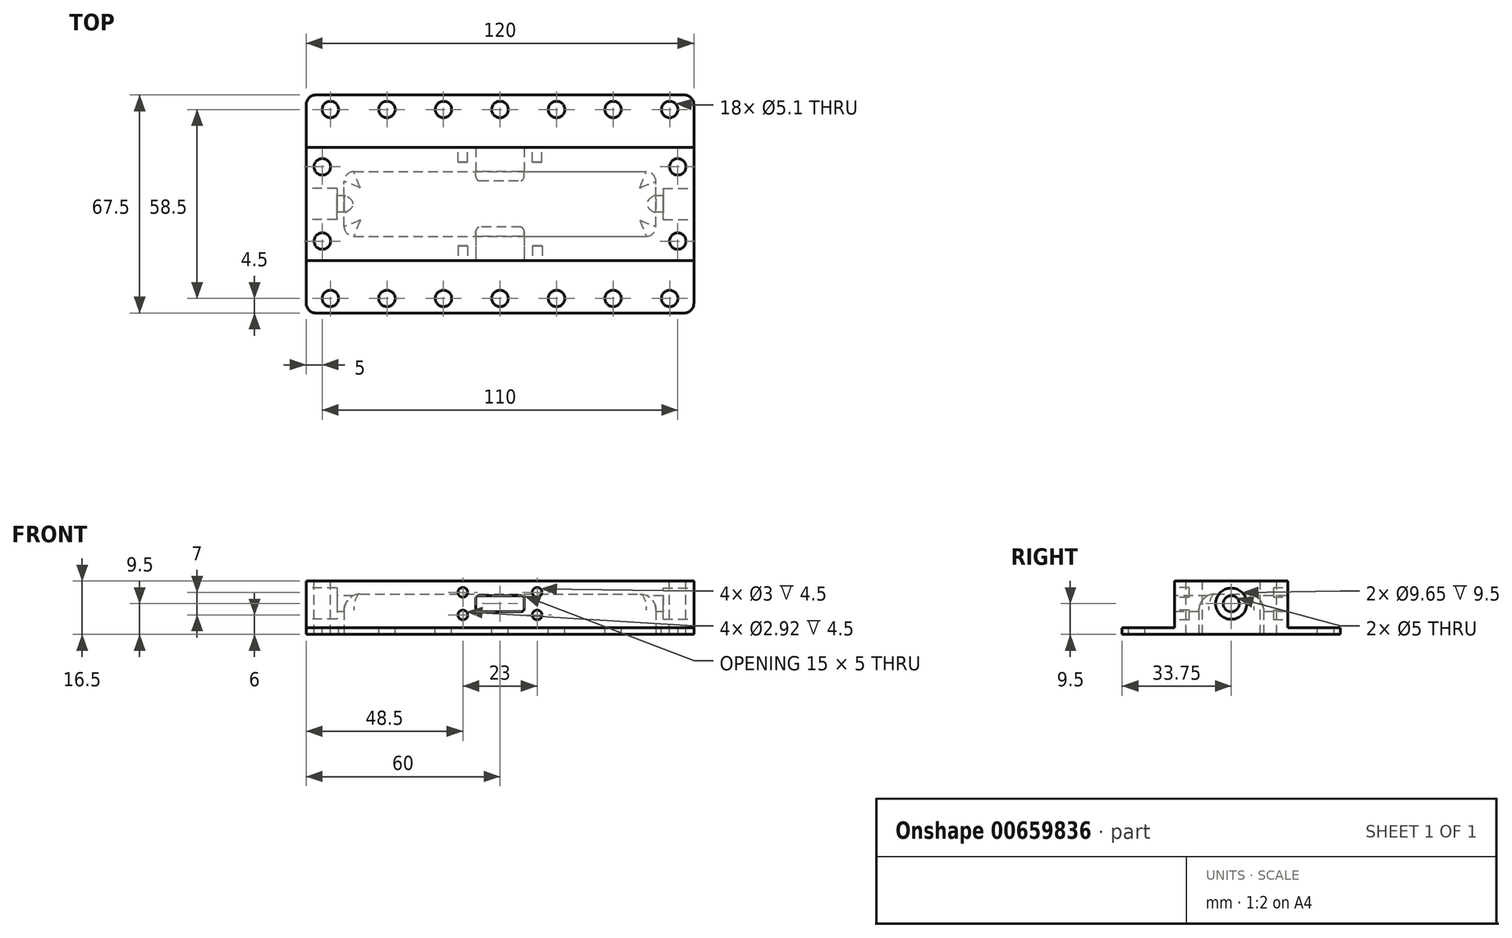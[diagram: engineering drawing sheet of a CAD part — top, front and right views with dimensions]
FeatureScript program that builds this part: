
annotation { "Feature Type Name" : "Feature", "Feature Type Description" : "" }
export const myFeature = defineFeature(function(context is Context, id is Id, definition is map)
    precondition{}
    {
        {
            var Q0;
            Q0=qCreatedBy(makeId("Top.planeOp"),FACE);
            var sketch = newSketch(context, id + "F0", { "sketchPlane" : qUnion([Q0])});
            skLineSegment(sketch, "E0.bottom", {"start": v(0, 0) * mm, "end": v(120, 0) * mm});
            skLineSegment(sketch, "E0.top", {"start": v(0, -67.5) * mm, "end": v(120, -67.5) * mm});
            skLineSegment(sketch, "E0.left", {"start": v(0, -67.5) * mm, "end": v(0, 0) * mm});
            skLineSegment(sketch, "E0.right", {"start": v(120, -67.5) * mm, "end": v(120, 0) * mm});
            skSolve(sketch);
        }
        {
            var Q0;
            Q0 = qSketchRegion(id + "F0", true);
            extrude(context, id + "F1", {"entities" : qUnion([Q0]), "oppositeDirection" : true, "depth" : 16.5 * mm, "offsetDistance" : 25 * mm});
        }
        {
            var Q0;
            Q0=makeQuery(id+"F1.opExtrude","CAP_FACE",FACE,{"disambiguationData":[OSD([sQuery(id+"F0.wireOp",EDGE,"E0.bottom"),sQuery(id+"F0.wireOp",EDGE,"E0.top"),sQuery(id+"F0.wireOp",EDGE,"E0.left"),sQuery(id+"F0.wireOp",EDGE,"E0.right")])],"isStart":false});
            var sketch = newSketch(context, id + "F2", { "sketchPlane" : qUnion([Q0])});
            skLineSegment(sketch, "E1.bottom", {"start": v(11.75, 43.75) * mm, "end": v(108.25, 43.75) * mm});
            skLineSegment(sketch, "E1.top", {"start": v(11.75, 23.75) * mm, "end": v(108.25, 23.75) * mm});
            skLineSegment(sketch, "E1.left", {"start": v(11.75, 43.75) * mm, "end": v(11.75, 23.75) * mm});
            skLineSegment(sketch, "E1.right", {"start": v(108.25, 43.75) * mm, "end": v(108.25, 23.75) * mm});
            skSolve(sketch);
        }
        {
            var Q0;
            Q0 = qSketchRegion(id + "F2", true);
            extrude(context, id + "F3", {"entities" : qUnion([Q0]), "operationType" : NewBodyOperationType.REMOVE, "oppositeDirection" : true, "depth" : 12.5 * mm, "offsetDistance" : 25 * mm});
        }
        {
            var Q0;
            Q0=makeQuery(id+"F1.opExtrude","CAP_FACE",FACE,{"disambiguationData":[OSD([sQuery(id+"F0.wireOp",EDGE,"E0.bottom"),sQuery(id+"F0.wireOp",EDGE,"E0.top"),sQuery(id+"F0.wireOp",EDGE,"E0.left"),sQuery(id+"F0.wireOp",EDGE,"E0.right")])],"isStart":true});
            var sketch = newSketch(context, id + "F4", { "sketchPlane" : qUnion([Q0])});
            skLineSegment(sketch, "E2.bottom", {"start": v(0, -16.25) * mm, "end": v(120, -16.25) * mm});
            skLineSegment(sketch, "E2.top", {"start": v(0, -51.25) * mm, "end": v(120, -51.25) * mm});
            skLineSegment(sketch, "E2.left", {"start": v(0, -16.25) * mm, "end": v(0, -51.25) * mm});
            skLineSegment(sketch, "E2.right", {"start": v(120, -16.25) * mm, "end": v(120, -51.25) * mm});
            skSolve(sketch);
        }
        {
            var Q0;
            Q0=makeQuery(id+"F4.imprint","IMPRINT",FACE,{"disambiguationData":[TD([[makeQuery(id+"F4.imprint","IMPRINT",EDGE,{"derivedFrom":sQuery(id+"F4.wireOp",EDGE,"E2.bottom")}),1.0]])]});
            var Q1;
            {var subQ0=sQuery(id+"F4.wireOp",EDGE,"E2.top");Q1=makeQuery(id+"F4.imprint","IMPRINT",FACE,{"disambiguationData":[TD([[makeQuery(id+"F4.imprint","IMPRINT",EDGE,{"derivedFrom":subQ0}),-1.0]])]});}
            extrude(context, id + "F5", {"entities" : qUnion([Q0, Q1]), "operationType" : NewBodyOperationType.REMOVE, "oppositeDirection" : true, "depth" : 14.5 * mm, "offsetDistance" : 25 * mm});
        }
        {
            var Q0;
            Q0=makeQuery(id+"F5.boolean.opBoolean","COPY",FACE,{"derivedFrom":makeQuery(id+"F5.opExtrude","SWEPT_FACE",FACE,{"disambiguationData":[OSD([sQuery(id+"F4.wireOp",EDGE,"E2.top")])]})});
            var sketch = newSketch(context, id + "F6", { "sketchPlane" : qUnion([Q0])});
            skLineSegment(sketch, "E3.bottom", {"start": v(52.5, -4.5) * mm, "end": v(67.5, -4.5) * mm});
            skLineSegment(sketch, "E3.top", {"start": v(52.5, -9.5) * mm, "end": v(67.5, -9.5) * mm});
            skLineSegment(sketch, "E3.left", {"start": v(52.5, -4.5) * mm, "end": v(52.5, -9.5) * mm});
            skLineSegment(sketch, "E3.right", {"start": v(67.5, -4.5) * mm, "end": v(67.5, -9.5) * mm});
            skSolve(sketch);
        }
        {
            var Q0;
            Q0 = qSketchRegion(id + "F6", true);
            extrude(context, id + "F7", {"entities" : qUnion([Q0]), "operationType" : NewBodyOperationType.REMOVE, "oppositeDirection" : true, "depth" : 39.7 * mm, "offsetDistance" : 25 * mm});
        }
        {
            var Q0;
            Q0=makeQuery(id+"F5.boolean.opBoolean","COPY",FACE,{"derivedFrom":makeQuery(id+"F5.opExtrude","CAP_FACE",FACE,{"disambiguationData":[OSD([sQuery(id+"F0.wireOp",EDGE,"E0.bottom"),sQuery(id+"F0.wireOp",EDGE,"E0.top"),sQuery(id+"F0.wireOp",EDGE,"E0.left"),sQuery(id+"F0.wireOp",EDGE,"E0.right"),sQuery(id+"F4.wireOp",EDGE,"E2.bottom"),sQuery(id+"F4.wireOp",EDGE,"E2.top"),sQuery(id+"F4.wireOp",EDGE,"E2.left"),sQuery(id+"F4.wireOp",EDGE,"E2.right")])],"isStart":false})});
            var sketch = newSketch(context, id + "F8", { "sketchPlane" : qUnion([Q0])});
            skCircle(sketch, "E4", {"center": v(7.5, -63) * mm, "radius": 2.55 * mm});
            skCircle(sketch, "E5.0.1.0", {"center": v(7.5, -4.5) * mm, "radius": 2.55 * mm});
            skCircle(sketch, "E5.1.0.0", {"center": v(25, -63) * mm, "radius": 2.55 * mm});
            skCircle(sketch, "E5.1.1.0", {"center": v(25, -4.5) * mm, "radius": 2.55 * mm});
            skCircle(sketch, "E5.2.0.0", {"center": v(42.5, -63) * mm, "radius": 2.55 * mm});
            skCircle(sketch, "E5.2.1.0", {"center": v(42.5, -4.5) * mm, "radius": 2.55 * mm});
            skLineSegment(sketch, "E5.direction1", {"start": v(7.5, -63) * mm, "end": v(25, -63) * mm, "construction": true});
            skLineSegment(sketch, "E5.direction2", {"start": v(7.5, -63) * mm, "end": v(7.5, -4.5) * mm, "construction": true});
            skCircle(sketch, "E6.0.3.0", {"center": v(60, -63) * mm, "radius": 2.55 * mm});
            skCircle(sketch, "E6.0.3.1", {"center": v(60, -4.5) * mm, "radius": 2.55 * mm});
            skCircle(sketch, "E6.0.4.0", {"center": v(77.5, -63) * mm, "radius": 2.55 * mm});
            skCircle(sketch, "E6.0.4.1", {"center": v(77.5, -4.5) * mm, "radius": 2.55 * mm});
            skCircle(sketch, "E6.0.5.0", {"center": v(95, -63) * mm, "radius": 2.55 * mm});
            skCircle(sketch, "E6.0.5.1", {"center": v(95, -4.5) * mm, "radius": 2.55 * mm});
            skCircle(sketch, "E6.0.6.0", {"center": v(112.5, -63) * mm, "radius": 2.55 * mm});
            skCircle(sketch, "E6.0.6.1", {"center": v(112.5, -4.5) * mm, "radius": 2.55 * mm});
            skCircle(sketch, "E7.2.0.0", {"center": v(240.5, -30) * mm, "radius": 1.6 * mm});
            skCircle(sketch, "E7.2.1.0", {"center": v(240.5, -10) * mm, "radius": 1.6 * mm});
            skSolve(sketch);
        }
        {
            var Q0;
            Q0 = qSketchRegion(id + "F8", true);
            extrude(context, id + "F9", {"entities" : qUnion([Q0]), "operationType" : NewBodyOperationType.REMOVE, "oppositeDirection" : true, "depth" : 25 * mm, "offsetDistance" : 25 * mm});
        }
        {
            var Q0;
            Q0=makeQuery(id+"F5.boolean.opBoolean","COPY",FACE,{"derivedFrom":makeQuery(id+"F5.opExtrude","SWEPT_FACE",FACE,{"disambiguationData":[OSD([sQuery(id+"F4.wireOp",EDGE,"E2.top")])]})});
            var sketch = newSketch(context, id + "F10", { "sketchPlane" : qUnion([Q0])});
            skCircle(sketch, "E8.1.0.0", {"center": v(48.5, -3.5) * mm, "radius": 1.5 * mm});
            skCircle(sketch, "E9.0.1.0", {"center": v(48.5, -10.5) * mm, "radius": 1.5 * mm});
            skCircle(sketch, "E9.1.0.0", {"center": v(71.5, -3.5) * mm, "radius": 1.5 * mm});
            skCircle(sketch, "E9.1.1.0", {"center": v(71.5, -10.5) * mm, "radius": 1.5 * mm});
            skLineSegment(sketch, "E9.direction1", {"start": v(48.5, -3.5) * mm, "end": v(71.5, -3.5) * mm, "construction": true});
            skLineSegment(sketch, "E9.direction2", {"start": v(48.5, -3.5) * mm, "end": v(48.5, -10.5) * mm, "construction": true});
            skSolve(sketch);
        }
        {
            var Q0;
            Q0 = qSketchRegion(id + "F10", true);
            extrude(context, id + "F11", {"entities" : qUnion([Q0]), "operationType" : NewBodyOperationType.REMOVE, "oppositeDirection" : true, "depth" : 4.5 * mm, "offsetDistance" : 25 * mm});
        }
        {
            var Q0;
            Q0=makeQuery(id+"F3.boolean.opBoolean","COPY",EDGE,{"derivedFrom":makeQuery(id+"F3.opExtrude","SWEPT_EDGE",EDGE,{"disambiguationData":[OSD([sQuery(id+"F2.wireOp",EDGE,"E1.bottom"),sQuery(id+"F2.wireOp",EDGE,"E1.left")])]})});
            var Q1;
            Q1=makeQuery(id+"F3.boolean.opBoolean","COPY",EDGE,{"derivedFrom":makeQuery(id+"F3.opExtrude","SWEPT_EDGE",EDGE,{"disambiguationData":[OSD([sQuery(id+"F2.wireOp",EDGE,"E1.bottom"),sQuery(id+"F2.wireOp",EDGE,"E1.right")])]})});
            var Q2;
            Q2=makeQuery(id+"F3.boolean.opBoolean","COPY",EDGE,{"derivedFrom":makeQuery(id+"F3.opExtrude","SWEPT_EDGE",EDGE,{"disambiguationData":[OSD([sQuery(id+"F2.wireOp",EDGE,"E1.top"),sQuery(id+"F2.wireOp",EDGE,"E1.right")])]})});
            var Q3;
            Q3=makeQuery(id+"F3.boolean.opBoolean","COPY",EDGE,{"derivedFrom":makeQuery(id+"F3.opExtrude","SWEPT_EDGE",EDGE,{"disambiguationData":[OSD([sQuery(id+"F2.wireOp",EDGE,"E1.top"),sQuery(id+"F2.wireOp",EDGE,"E1.left")])]})});
            fillet(context, id + "F12", {"entities" : qUnion([Q0, Q1, Q2, Q3]), "radius" : 3 * mm, "tangentPropagation" : true, "allowEdgeOverflow" : false});
        }
        {
            var Q0;
            Q0=makeQuery(id+"F3.boolean.opBoolean","COPY",EDGE,{"derivedFrom":makeQuery(id+"F3.opExtrude","CAP_EDGE",EDGE,{"disambiguationData":[OSD([sQuery(id+"F2.wireOp",EDGE,"E1.bottom")])],"isStart":false})});
            var Q1;
            Q1=makeQuery(id+"F3.boolean.opBoolean","COPY",EDGE,{"derivedFrom":makeQuery(id+"F3.opExtrude","CAP_EDGE",EDGE,{"disambiguationData":[OSD([sQuery(id+"F2.wireOp",EDGE,"E1.top")])],"isStart":false})});
            fillet(context, id + "F13", {"entities" : qUnion([Q0, Q1]), "radius" : 5 * mm, "tangentPropagation" : true, "allowEdgeOverflow" : false});
        }
        {
            var Q0;
            {var subQ0=sQuery(id+"F6.wireOp",EDGE,"E3.top");var subQ1=sQuery(id+"F6.wireOp",EDGE,"E3.left");Q0=makeQuery(id+"F7.boolean.opBoolean","COPY",EDGE,{"disambiguationData":[TD([makeQuery(id+"F3.boolean.opBoolean","COPY",FACE,{"derivedFrom":makeQuery(id+"F3.opExtrude","SWEPT_FACE",FACE,{"disambiguationData":[OSD([sQuery(id+"F2.wireOp",EDGE,"E1.bottom")])]})})])],"derivedFrom":makeQuery(id+"F7.opExtrude","SWEPT_EDGE",EDGE,{"disambiguationData":[OSD([subQ0,subQ1])]})});}
            var Q1;
            {var subQ0=sQuery(id+"F6.wireOp",EDGE,"E3.left");var subQ1=sQuery(id+"F6.wireOp",EDGE,"E3.bottom");Q1=makeQuery(id+"F7.boolean.opBoolean","COPY",EDGE,{"disambiguationData":[TD([makeQuery(id+"F3.boolean.opBoolean","COPY",FACE,{"derivedFrom":makeQuery(id+"F3.opExtrude","SWEPT_FACE",FACE,{"disambiguationData":[OSD([sQuery(id+"F2.wireOp",EDGE,"E1.bottom")])]})})])],"derivedFrom":makeQuery(id+"F7.opExtrude","SWEPT_EDGE",EDGE,{"disambiguationData":[OSD([subQ1,subQ0])]})});}
            var Q2;
            {var subQ0=sQuery(id+"F6.wireOp",EDGE,"E3.bottom");var subQ1=sQuery(id+"F6.wireOp",EDGE,"E3.right");Q2=makeQuery(id+"F7.boolean.opBoolean","COPY",EDGE,{"disambiguationData":[TD([makeQuery(id+"F3.boolean.opBoolean","COPY",FACE,{"derivedFrom":makeQuery(id+"F3.opExtrude","SWEPT_FACE",FACE,{"disambiguationData":[OSD([sQuery(id+"F2.wireOp",EDGE,"E1.bottom")])]})})])],"derivedFrom":makeQuery(id+"F7.opExtrude","SWEPT_EDGE",EDGE,{"disambiguationData":[OSD([subQ0,subQ1])]})});}
            var Q3;
            {var subQ0=sQuery(id+"F6.wireOp",EDGE,"E3.top");var subQ1=sQuery(id+"F6.wireOp",EDGE,"E3.right");Q3=makeQuery(id+"F7.boolean.opBoolean","COPY",EDGE,{"disambiguationData":[TD([makeQuery(id+"F3.boolean.opBoolean","COPY",FACE,{"derivedFrom":makeQuery(id+"F3.opExtrude","SWEPT_FACE",FACE,{"disambiguationData":[OSD([sQuery(id+"F2.wireOp",EDGE,"E1.bottom")])]})})])],"derivedFrom":makeQuery(id+"F7.opExtrude","SWEPT_EDGE",EDGE,{"disambiguationData":[OSD([subQ0,subQ1])]})});}
            fillet(context, id + "F14", {"entities" : qUnion([Q0, Q1, Q2, Q3]), "radius" : 1 * mm, "tangentPropagation" : true, "allowEdgeOverflow" : false});
        }
        {
            var Q0;
            {var subQ0=sQuery(id+"F6.wireOp",EDGE,"E3.right");var subQ1=sQuery(id+"F6.wireOp",EDGE,"E3.top");Q0=makeQuery(id+"F7.boolean.opBoolean","COPY",EDGE,{"disambiguationData":[TD([makeQuery(id+"F3.boolean.opBoolean","COPY",FACE,{"derivedFrom":makeQuery(id+"F3.opExtrude","SWEPT_FACE",FACE,{"disambiguationData":[OSD([sQuery(id+"F2.wireOp",EDGE,"E1.top")])]})})])],"derivedFrom":makeQuery(id+"F7.opExtrude","SWEPT_EDGE",EDGE,{"disambiguationData":[OSD([subQ1,subQ0])]})});}
            var Q1;
            {var subQ0=sQuery(id+"F6.wireOp",EDGE,"E3.top");var subQ1=sQuery(id+"F6.wireOp",EDGE,"E3.left");Q1=makeQuery(id+"F7.boolean.opBoolean","COPY",EDGE,{"disambiguationData":[TD([makeQuery(id+"F3.boolean.opBoolean","COPY",FACE,{"derivedFrom":makeQuery(id+"F3.opExtrude","SWEPT_FACE",FACE,{"disambiguationData":[OSD([sQuery(id+"F2.wireOp",EDGE,"E1.top")])]})})])],"derivedFrom":makeQuery(id+"F7.opExtrude","SWEPT_EDGE",EDGE,{"disambiguationData":[OSD([subQ0,subQ1])]})});}
            var Q2;
            {var subQ0=sQuery(id+"F6.wireOp",EDGE,"E3.bottom");var subQ1=sQuery(id+"F6.wireOp",EDGE,"E3.left");Q2=makeQuery(id+"F7.boolean.opBoolean","COPY",EDGE,{"disambiguationData":[TD([makeQuery(id+"F3.boolean.opBoolean","COPY",FACE,{"derivedFrom":makeQuery(id+"F3.opExtrude","SWEPT_FACE",FACE,{"disambiguationData":[OSD([sQuery(id+"F2.wireOp",EDGE,"E1.top")])]})})])],"derivedFrom":makeQuery(id+"F7.opExtrude","SWEPT_EDGE",EDGE,{"disambiguationData":[OSD([subQ0,subQ1])]})});}
            var Q3;
            {var subQ0=sQuery(id+"F6.wireOp",EDGE,"E3.bottom");var subQ1=sQuery(id+"F6.wireOp",EDGE,"E3.right");Q3=makeQuery(id+"F7.boolean.opBoolean","COPY",EDGE,{"disambiguationData":[TD([makeQuery(id+"F3.boolean.opBoolean","COPY",FACE,{"derivedFrom":makeQuery(id+"F3.opExtrude","SWEPT_FACE",FACE,{"disambiguationData":[OSD([sQuery(id+"F2.wireOp",EDGE,"E1.top")])]})})])],"derivedFrom":makeQuery(id+"F7.opExtrude","SWEPT_EDGE",EDGE,{"disambiguationData":[OSD([subQ0,subQ1])]})});}
            fillet(context, id + "F15", {"entities" : qUnion([Q0, Q1, Q2, Q3]), "radius" : 1 * mm, "tangentPropagation" : true, "allowEdgeOverflow" : false});
        }
        {
            var Q0;
            Q0=makeQuery(id+"F1.opExtrude","SWEPT_EDGE",EDGE,{"disambiguationData":[OSD([sQuery(id+"F0.wireOp",EDGE,"E0.bottom"),sQuery(id+"F0.wireOp",EDGE,"E0.right")])]});
            var Q1;
            Q1=makeQuery(id+"F1.opExtrude","SWEPT_EDGE",EDGE,{"disambiguationData":[OSD([sQuery(id+"F0.wireOp",EDGE,"E0.top"),sQuery(id+"F0.wireOp",EDGE,"E0.right")])]});
            var Q2;
            Q2=makeQuery(id+"F1.opExtrude","SWEPT_EDGE",EDGE,{"disambiguationData":[OSD([sQuery(id+"F0.wireOp",EDGE,"E0.bottom"),sQuery(id+"F0.wireOp",EDGE,"E0.left")])]});
            var Q3;
            Q3=makeQuery(id+"F1.opExtrude","SWEPT_EDGE",EDGE,{"disambiguationData":[OSD([sQuery(id+"F0.wireOp",EDGE,"E0.top"),sQuery(id+"F0.wireOp",EDGE,"E0.left")])]});
            fillet(context, id + "F16", {"entities" : qUnion([Q0, Q1, Q2, Q3]), "radius" : 3 * mm, "tangentPropagation" : true, "allowEdgeOverflow" : false});
        }
        {
            var Q0;
            Q0=makeQuery(id+"F5.boolean.opBoolean","COPY",FACE,{"derivedFrom":makeQuery(id+"F5.opExtrude","SWEPT_FACE",FACE,{"disambiguationData":[OSD([sQuery(id+"F4.wireOp",EDGE,"E2.bottom")])]})});
            var sketch = newSketch(context, id + "F17", { "sketchPlane" : qUnion([Q0])});
            skCircle(sketch, "E10", {"center": v(-71.5, -3.5) * mm, "radius": 1.46 * mm});
            skCircle(sketch, "E11.0.1.0", {"center": v(-71.5, -10.5) * mm, "radius": 1.46 * mm});
            skCircle(sketch, "E11.1.0.0", {"center": v(-48.5, -3.5) * mm, "radius": 1.46 * mm});
            skCircle(sketch, "E11.1.1.0", {"center": v(-48.5, -10.5) * mm, "radius": 1.46 * mm});
            skLineSegment(sketch, "E11.direction1", {"start": v(-71.5, -3.5) * mm, "end": v(-48.5, -3.5) * mm, "construction": true});
            skLineSegment(sketch, "E11.direction2", {"start": v(-71.5, -3.5) * mm, "end": v(-71.5, -10.5) * mm, "construction": true});
            skSolve(sketch);
        }
        {
            var Q0;
            Q0 = qSketchRegion(id + "F17", true);
            extrude(context, id + "F18", {"entities" : qUnion([Q0]), "operationType" : NewBodyOperationType.REMOVE, "oppositeDirection" : true, "depth" : 4.5 * mm, "offsetDistance" : 25 * mm});
        }
        {
            var Q0;
            Q0=makeQuery(id+"F1.opExtrude","SWEPT_FACE",FACE,{"disambiguationData":[OSD([sQuery(id+"F0.wireOp",EDGE,"E0.left")])]});
            var sketch = newSketch(context, id + "F19", { "sketchPlane" : qUnion([Q0])});
            skCircle(sketch, "E12", {"center": v(33.75, -7) * mm, "radius": 4.83 * mm});
            skSolve(sketch);
        }
        {
            var Q0;
            Q0 = qSketchRegion(id + "F19", true);
            extrude(context, id + "F20", {"entities" : qUnion([Q0]), "operationType" : NewBodyOperationType.REMOVE, "oppositeDirection" : true, "depth" : 9.5 * mm, "offsetDistance" : 25 * mm});
        }
        {
            var Q0;
            Q0=makeQuery(id+"F1.opExtrude","SWEPT_FACE",FACE,{"disambiguationData":[OSD([sQuery(id+"F0.wireOp",EDGE,"E0.right")])]});
            var sketch = newSketch(context, id + "F21", { "sketchPlane" : qUnion([Q0])});
            skCircle(sketch, "E13", {"center": v(-33.75, -7) * mm, "radius": 4.83 * mm});
            skSolve(sketch);
        }
        {
            var Q0;
            Q0 = qSketchRegion(id + "F21", true);
            extrude(context, id + "F22", {"entities" : qUnion([Q0]), "operationType" : NewBodyOperationType.REMOVE, "oppositeDirection" : true, "depth" : 9.5 * mm, "offsetDistance" : 25 * mm});
        }
        {
            var Q0;
            Q0=makeQuery(id+"F20.boolean.opBoolean","COPY",FACE,{"derivedFrom":makeQuery(id+"F20.opExtrude","CAP_FACE",FACE,{"disambiguationData":[OSD([sQuery(id+"F19.wireOp",EDGE,"E12")])],"isStart":false})});
            var sketch = newSketch(context, id + "F23", { "sketchPlane" : qUnion([Q0])});
            skCircle(sketch, "E14", {"center": v(33.75, -7) * mm, "radius": 2.5 * mm});
            skSolve(sketch);
        }
        {
            var Q0;
            Q0 = qSketchRegion(id + "F23", true);
            extrude(context, id + "F24", {"entities" : qUnion([Q0]), "operationType" : NewBodyOperationType.REMOVE, "oppositeDirection" : true, "depth" : 114 * mm, "offsetDistance" : 25 * mm});
        }
        {
            var Q0;
            Q0=makeQuery(id+"F1.opExtrude","CAP_FACE",FACE,{"disambiguationData":[OSD([sQuery(id+"F0.wireOp",EDGE,"E0.bottom"),sQuery(id+"F0.wireOp",EDGE,"E0.top"),sQuery(id+"F0.wireOp",EDGE,"E0.left"),sQuery(id+"F0.wireOp",EDGE,"E0.right")])],"isStart":true});
            var sketch = newSketch(context, id + "F25", { "sketchPlane" : qUnion([Q0])});
            skCircle(sketch, "E15", {"center": v(5, -45.25) * mm, "radius": 2.55 * mm});
            skCircle(sketch, "E16", {"center": v(5, -22.25) * mm, "radius": 2.55 * mm});
            skCircle(sketch, "E17.1.0.0", {"center": v(115, -22.25) * mm, "radius": 2.55 * mm});
            skCircle(sketch, "E17.1.0.1", {"center": v(115, -45.25) * mm, "radius": 2.55 * mm});
            skLineSegment(sketch, "E17.direction1", {"start": v(5, -22.25) * mm, "end": v(115, -22.25) * mm, "construction": true});
            skSolve(sketch);
        }
        {
            var Q0;
            Q0 = qSketchRegion(id + "F25", true);
            extrude(context, id + "F26", {"entities" : qUnion([Q0]), "operationType" : NewBodyOperationType.REMOVE, "oppositeDirection" : true, "depth" : 43.3 * mm, "offsetDistance" : 25 * mm});
        }
    });
